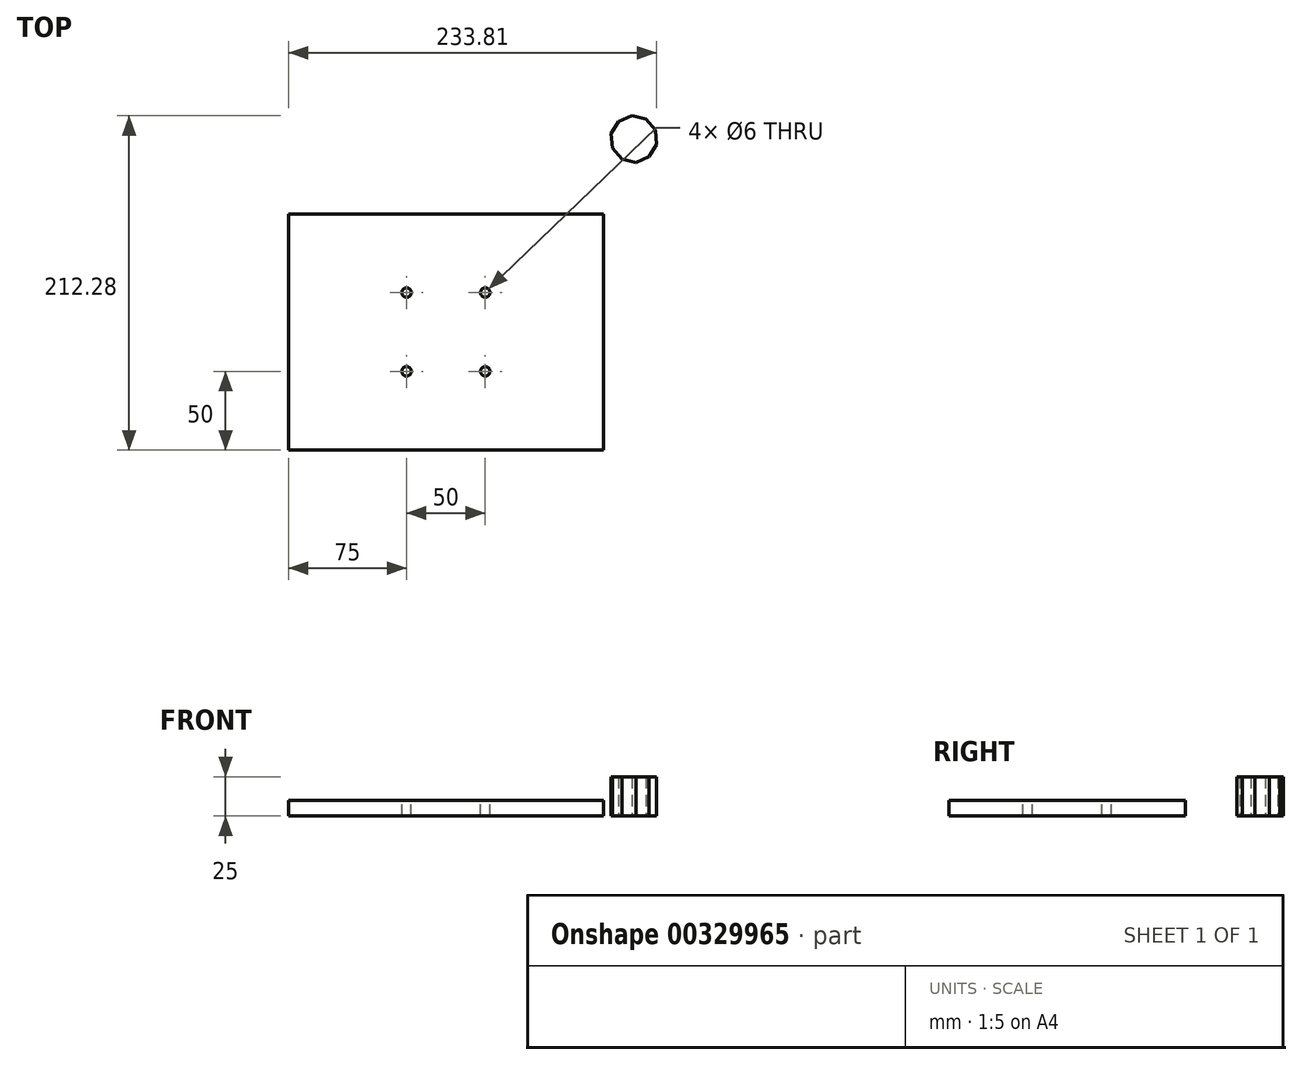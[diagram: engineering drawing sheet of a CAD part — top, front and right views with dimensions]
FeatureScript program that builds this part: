
annotation { "Feature Type Name" : "Feature", "Feature Type Description" : "" }
export const myFeature = defineFeature(function(context is Context, id is Id, definition is map)
    precondition{}
    {
        {
            var Q0;
            Q0=qCreatedBy(makeId("Top.planeOp"),FACE);
            var sketch = newSketch(context, id + "F0", { "sketchPlane" : qUnion([Q0])});
            skLineSegment(sketch, "E0.bottom", {"start": v(-200, 0) * mm, "end": v(0, 0) * mm});
            skLineSegment(sketch, "E0.top", {"start": v(-200, -150) * mm, "end": v(0, -150) * mm});
            skLineSegment(sketch, "E0.left", {"start": v(-200, 0) * mm, "end": v(-200, -150) * mm});
            skLineSegment(sketch, "E0.right", {"start": v(0, 0) * mm, "end": v(0, -150) * mm});
            skSolve(sketch);
        }
        {
            var Q0;
            Q0=makeQuery(id+"F0.imprint","IMPRINT",FACE,{"disambiguationData":[TD([[makeQuery(id+"F0.imprint","IMPRINT",EDGE,{"derivedFrom":sQuery(id+"F0.wireOp",EDGE,"E0.bottom")}),-1.0]])]});
            extrude(context, id + "F1", {"entities" : qUnion([Q0]), "depth" : 10 * mm});
        }
        {
            var Q0;
            Q0=makeQuery(id+"F1.opExtrude","CAP_FACE",FACE,{"disambiguationData":[OSD([sQuery(id+"F0.wireOp",EDGE,"E0.bottom"),sQuery(id+"F0.wireOp",EDGE,"E0.top"),sQuery(id+"F0.wireOp",EDGE,"E0.left"),sQuery(id+"F0.wireOp",EDGE,"E0.right")])],"isStart":false});
            var sketch = newSketch(context, id + "F2", { "sketchPlane" : qUnion([Q0])});
            skPoint(sketch, "E1", {"position": v(-125, -50) * mm});
            skPoint(sketch, "E2", {"position": v(-75, -50) * mm});
            skPoint(sketch, "E3", {"position": v(-125, -100) * mm});
            skPoint(sketch, "E4", {"position": v(-75, -100) * mm});
            skSolve(sketch);
        }
        {
            var Q0;
            Q0=sQuery(id+"F2.wireOp",VERTEX,"E1");
            var Q1;
            Q1=sQuery(id+"F2.wireOp",VERTEX,"E2");
            var Q2;
            Q2=sQuery(id+"F2.wireOp",VERTEX,"E4");
            var Q3;
            Q3=sQuery(id+"F2.wireOp",VERTEX,"E3");
            var Q4;
            Q4=makeQuery(id+"F1.opExtrude","SWEPT_BODY",BODY,{"disambiguationData":[OSD([sQuery(id+"F0.wireOp",EDGE,"E0.bottom"),sQuery(id+"F0.wireOp",EDGE,"E0.top"),sQuery(id+"F0.wireOp",EDGE,"E0.left"),sQuery(id+"F0.wireOp",EDGE,"E0.right")])]});
            hole(context, id + "F3", {"style" : HoleStyle.SIMPLE, "endStyle" : HoleEndStyle.THROUGH, "holeDiameter" : 6 * mm, "tappedDepth" : 12.7 * mm, "tapClearance" : 3, "locations" : qUnion([Q0, Q1, Q2, Q3]), "scope" : qUnion([Q4])});
        }
        {
            var Q0;
            Q0=qCreatedBy(makeId("Top.planeOp"),FACE);
            var sketch = newSketch(context, id + "F4", { "sketchPlane" : qUnion([Q0])});
            skCircle(sketch, "E5.cCircle", {"center": v(19.36, 47.5) * mm, "radius": 14.84 * mm, "construction": true});
            skLineSegment(sketch, "E5.0", {"start": v(20.65, 32.72) * mm, "end": v(11.71, 34.79) * mm});
            skLineSegment(sketch, "E5.1", {"start": v(11.71, 34.79) * mm, "end": v(5.7, 41.7) * mm});
            skLineSegment(sketch, "E5.2", {"start": v(5.7, 41.7) * mm, "end": v(4.9, 50.84) * mm});
            skLineSegment(sketch, "E5.3", {"start": v(4.9, 50.84) * mm, "end": v(9.62, 58.7) * mm});
            skLineSegment(sketch, "E5.4", {"start": v(9.62, 58.7) * mm, "end": v(18.07, 62.28) * mm});
            skLineSegment(sketch, "E5.5", {"start": v(18.07, 62.28) * mm, "end": v(27, 60.22) * mm});
            skLineSegment(sketch, "E5.6", {"start": v(27, 60.22) * mm, "end": v(33.01, 53.3) * mm});
            skLineSegment(sketch, "E5.7", {"start": v(33.01, 53.3) * mm, "end": v(33.81, 44.16) * mm});
            skLineSegment(sketch, "E5.8", {"start": v(33.81, 44.16) * mm, "end": v(29.09, 36.3) * mm});
            skLineSegment(sketch, "E5.9", {"start": v(29.09, 36.3) * mm, "end": v(20.65, 32.72) * mm});
            skSolve(sketch);
        }
        {
            var Q0;
            Q0=makeQuery(id+"F4.imprint","IMPRINT",FACE,{"disambiguationData":[TD([[makeQuery(id+"F4.imprint","IMPRINT",EDGE,{"derivedFrom":sQuery(id+"F4.wireOp",EDGE,"E5.0")}),-1.0]])]});
            extrude(context, id + "F5", {"entities" : qUnion([Q0]), "depth" : 25 * mm});
        }
    });
